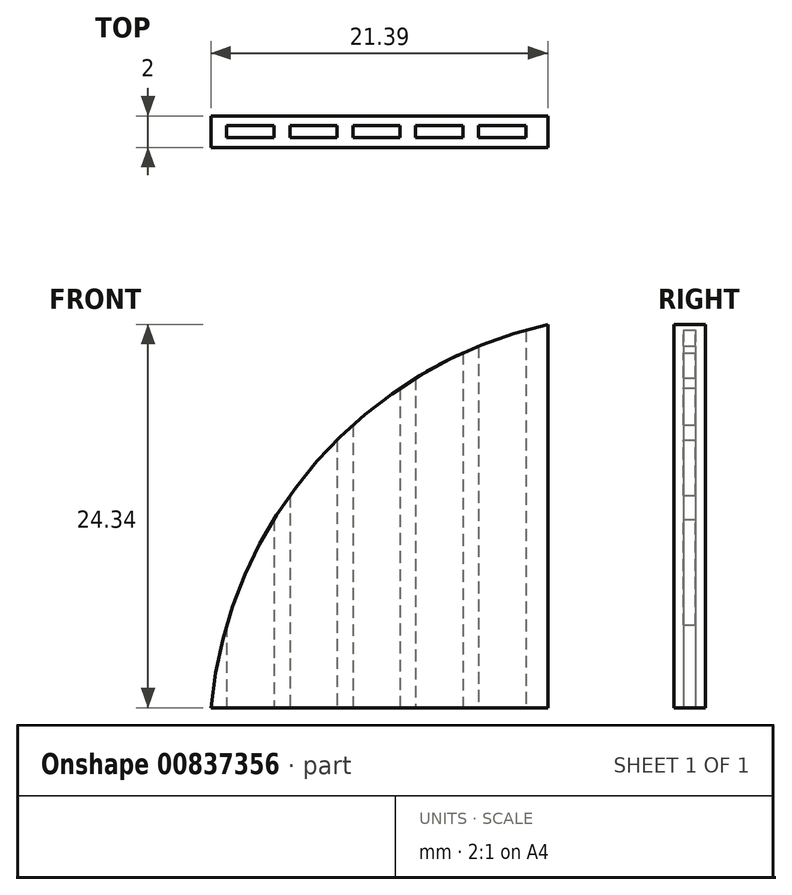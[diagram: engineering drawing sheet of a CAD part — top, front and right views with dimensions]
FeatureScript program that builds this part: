
annotation { "Feature Type Name" : "Feature", "Feature Type Description" : "" }
export const myFeature = defineFeature(function(context is Context, id is Id, definition is map)
    precondition{}
    {
        {
            var Q0;
            Q0=qCreatedBy(makeId("Front.planeOp"),FACE);
            var sketch = newSketch(context, id + "F0", { "sketchPlane" : qUnion([Q0])});
            skArc(sketch, "E0", {"start": v(-6, 26.84) * mm, "mid": v(-20.66, 18.15) * mm, "end": v(-27.39, 2.5) * mm});
            skLineSegment(sketch, "E1", {"start": v(-27.39, 2.5) * mm, "end": v(-6, 2.5) * mm});
            skLineSegment(sketch, "E2", {"start": v(-6, 2.5) * mm, "end": v(-6, 26.84) * mm});
            skSolve(sketch);
        }
        {
            var Q0;
            Q0=makeQuery(id+"F0.imprint","IMPRINT",FACE,{"disambiguationData":[TD([[makeQuery(id+"F0.imprint","IMPRINT",EDGE,{"derivedFrom":sQuery(id+"F0.wireOp",EDGE,"E0")}),1.0]])]});
            extrude(context, id + "F1", {"entities" : qUnion([Q0]), "depth" : 2 * mm, "offsetDistance" : 25 * mm});
        }
        {
            var Q0;
            Q0=makeQuery(id+"F1.opExtrude","SWEPT_FACE",FACE,{"disambiguationData":[OSD([sQuery(id+"F0.wireOp",EDGE,"E1")])]});
            var sketch = newSketch(context, id + "F2", { "sketchPlane" : qUnion([Q0])});
            skLineSegment(sketch, "E3.bottom", {"start": v(-26.39, 1.38) * mm, "end": v(-23.39, 1.38) * mm});
            skLineSegment(sketch, "E3.top", {"start": v(-26.39, 0.62) * mm, "end": v(-23.39, 0.62) * mm});
            skLineSegment(sketch, "E3.left", {"start": v(-26.39, 1.38) * mm, "end": v(-26.39, 0.62) * mm});
            skLineSegment(sketch, "E3.right", {"start": v(-23.39, 1.38) * mm, "end": v(-23.39, 0.62) * mm});
            skLineSegment(sketch, "E4", {"start": v(-26.39, 1.38) * mm, "end": v(-26.39, 2) * mm, "construction": true});
            skLineSegment(sketch, "E5", {"start": v(-26.39, 0.62) * mm, "end": v(-26.39, 0) * mm, "construction": true});
            skLineSegment(sketch, "E6.1.0.0", {"start": v(-22.39, 0.62) * mm, "end": v(-19.39, 0.62) * mm});
            skLineSegment(sketch, "E6.1.0.1", {"start": v(-22.39, 1.38) * mm, "end": v(-22.39, 0.62) * mm});
            skLineSegment(sketch, "E6.1.0.2", {"start": v(-19.39, 1.38) * mm, "end": v(-19.39, 0.62) * mm});
            skLineSegment(sketch, "E6.1.0.3", {"start": v(-22.39, 1.38) * mm, "end": v(-19.39, 1.38) * mm});
            skLineSegment(sketch, "E6.2.0.0", {"start": v(-18.39, 0.62) * mm, "end": v(-15.39, 0.62) * mm});
            skLineSegment(sketch, "E6.2.0.1", {"start": v(-18.39, 1.38) * mm, "end": v(-18.39, 0.62) * mm});
            skLineSegment(sketch, "E6.2.0.2", {"start": v(-15.39, 1.38) * mm, "end": v(-15.39, 0.62) * mm});
            skLineSegment(sketch, "E6.2.0.3", {"start": v(-18.39, 1.38) * mm, "end": v(-15.39, 1.38) * mm});
            skLineSegment(sketch, "E6.3.0.0", {"start": v(-14.39, 0.62) * mm, "end": v(-11.39, 0.62) * mm});
            skLineSegment(sketch, "E6.3.0.1", {"start": v(-14.39, 1.38) * mm, "end": v(-14.39, 0.62) * mm});
            skLineSegment(sketch, "E6.3.0.2", {"start": v(-11.39, 1.38) * mm, "end": v(-11.39, 0.62) * mm});
            skLineSegment(sketch, "E6.3.0.3", {"start": v(-14.39, 1.38) * mm, "end": v(-11.39, 1.38) * mm});
            skLineSegment(sketch, "E6.4.0.0", {"start": v(-10.39, 0.62) * mm, "end": v(-7.39, 0.62) * mm});
            skLineSegment(sketch, "E6.4.0.1", {"start": v(-10.39, 1.38) * mm, "end": v(-10.39, 0.62) * mm});
            skLineSegment(sketch, "E6.4.0.2", {"start": v(-7.39, 1.38) * mm, "end": v(-7.39, 0.62) * mm});
            skLineSegment(sketch, "E6.4.0.3", {"start": v(-10.39, 1.38) * mm, "end": v(-7.39, 1.38) * mm});
            skLineSegment(sketch, "E6.direction1", {"start": v(-26.39, 0.62) * mm, "end": v(-22.39, 0.62) * mm, "construction": true});
            skSolve(sketch);
        }
        {
            var Q0;
            Q0=makeQuery(id+"F2.imprint","IMPRINT",FACE,{"disambiguationData":[TD([[makeQuery(id+"F2.imprint","IMPRINT",EDGE,{"derivedFrom":sQuery(id+"F2.wireOp",EDGE,"E3.bottom")}),-1.0]])]});
            var Q1;
            Q1=makeQuery(id+"F2.imprint","IMPRINT",FACE,{"disambiguationData":[TD([[makeQuery(id+"F2.imprint","IMPRINT",EDGE,{"derivedFrom":sQuery(id+"F2.wireOp",EDGE,"E6.1.0.0")}),1.0]])]});
            var Q2;
            Q2=makeQuery(id+"F2.imprint","IMPRINT",FACE,{"disambiguationData":[TD([[makeQuery(id+"F2.imprint","IMPRINT",EDGE,{"derivedFrom":sQuery(id+"F2.wireOp",EDGE,"E6.2.0.0")}),1.0]])]});
            var Q3;
            Q3=makeQuery(id+"F2.imprint","IMPRINT",FACE,{"disambiguationData":[TD([[makeQuery(id+"F2.imprint","IMPRINT",EDGE,{"derivedFrom":sQuery(id+"F2.wireOp",EDGE,"E6.3.0.0")}),1.0]])]});
            var Q4;
            Q4=makeQuery(id+"F2.imprint","IMPRINT",FACE,{"disambiguationData":[TD([[makeQuery(id+"F2.imprint","IMPRINT",EDGE,{"derivedFrom":sQuery(id+"F2.wireOp",EDGE,"E6.4.0.0")}),1.0]])]});
            extrude(context, id + "F3", {"entities" : qUnion([Q0, Q1, Q2, Q3, Q4]), "operationType" : NewBodyOperationType.REMOVE, "oppositeDirection" : true, "depth" : 25 * mm, "offsetDistance" : 25 * mm});
        }
    });
